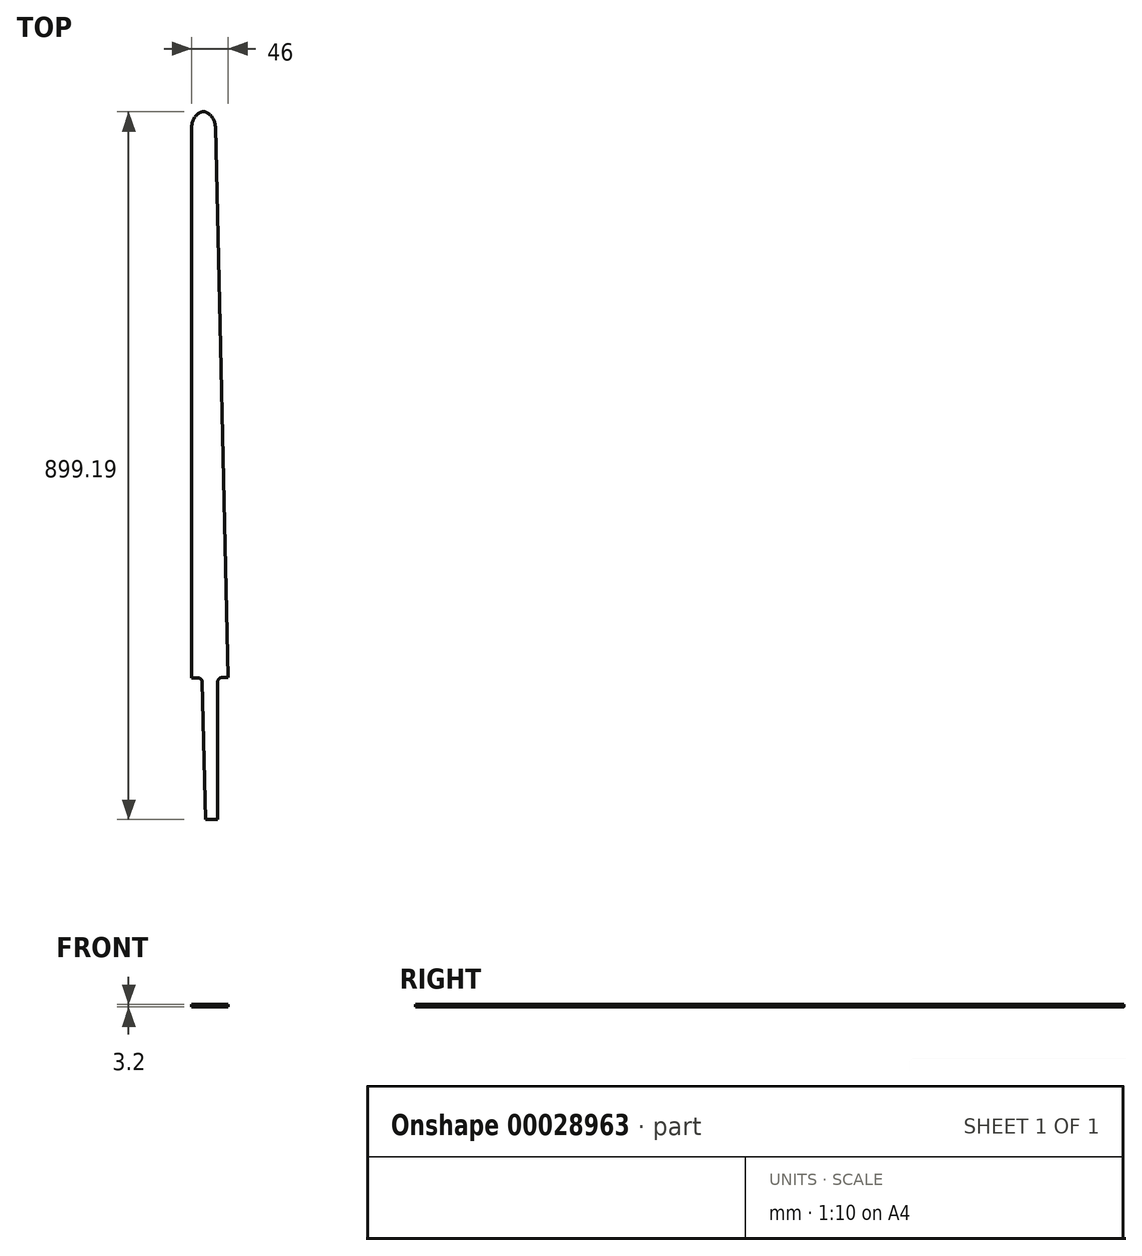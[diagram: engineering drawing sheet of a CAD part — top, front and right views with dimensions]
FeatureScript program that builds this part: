
annotation { "Feature Type Name" : "Feature", "Feature Type Description" : "" }
export const myFeature = defineFeature(function(context is Context, id is Id, definition is map)
    precondition{}
    {
        {
            var Q0;
            Q0=qCreatedBy(makeId("Top.planeOp"),FACE);
            var sketch = newSketch(context, id + "F0", { "sketchPlane" : qUnion([Q0])});
            skLineSegment(sketch, "E0", {"start": v(-23, 430.96) * mm, "end": v(-23, -269.34) * mm});
            skLineSegment(sketch, "E1", {"start": v(-23, -269.34) * mm, "end": v(-14.93, -269.25) * mm});
            skLineSegment(sketch, "E2", {"start": v(-9.87, -274.12) * mm, "end": v(-5.44, -449.15) * mm});
            skLineSegment(sketch, "E3", {"start": v(-5.44, -449.15) * mm, "end": v(9.56, -448.98) * mm});
            skLineSegment(sketch, "E4", {"start": v(9.56, -448.98) * mm, "end": v(9.99, -273.9) * mm});
            skLineSegment(sketch, "E5", {"start": v(14.93, -268.9) * mm, "end": v(23, -268.81) * mm});
            skLineSegment(sketch, "E6", {"start": v(23, -268.81) * mm, "end": v(7, 431.05) * mm});
            skArc(sketch, "E7", {"start": v(7, 431.05) * mm, "mid": v(4.27, 441) * mm, "end": v(-2.82, 448.5) * mm});
            skArc(sketch, "E8", {"start": v(-23, 430.96) * mm, "mid": v(-20.5, 440.86) * mm, "end": v(-13.57, 448.38) * mm});
            skArc(sketch, "E9", {"start": v(-2.82, 448.5) * mm, "mid": v(-8.22, 450.04) * mm, "end": v(-13.57, 448.38) * mm});
            skArc(sketch, "E10", {"start": v(-9.87, -274.12) * mm, "mid": v(-11.4, -270.65) * mm, "end": v(-14.93, -269.25) * mm});
            skArc(sketch, "E11", {"start": v(14.93, -268.9) * mm, "mid": v(11.44, -270.39) * mm, "end": v(9.99, -273.9) * mm});
            skSolve(sketch);
        }
        {
            var Q0;
            Q0=makeQuery(id+"F0.imprint","IMPRINT",FACE,{"disambiguationData":[TD([[makeQuery(id+"F0.imprint","IMPRINT",EDGE,{"derivedFrom":sQuery(id+"F0.wireOp",EDGE,"E0")}),1.0]])]});
            extrude(context, id + "F1", {"entities" : qUnion([Q0]), "depth" : 3.2 * mm});
        }
    });
